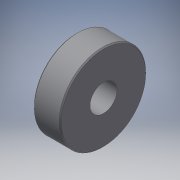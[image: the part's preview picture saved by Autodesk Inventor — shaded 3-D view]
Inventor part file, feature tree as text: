
AUTODESK INVENTOR PART (.ipt)
format: ipt  version: 2019 (Build 230136000, 136)  size: 109,568 bytes
history: native  units: in
note: dims shown in document units (in); Inventor stores cm internally (conversion verified against a paired STEP export)
features: extrude x1, chamfer x1, sketch x1
ambient origin geometry x8: Origin, YZ Plane, XZ Plane, XY Plane, X Axis, Y Axis, Z Axis, Center Point
bodies: Solid1 (feature_tree)
feature tree (3):
  extrude  "Extrusion1"  Depth=0.1969in
  chamfer  "Chamfer1"  Distance=0.1969in
  sketch  "Sketch1"  dims[d0=0.6299in d1=0.1969in d2=0.1969in d3=0.0in d4=0.0079in d5=0.125in d6=45.0deg]
